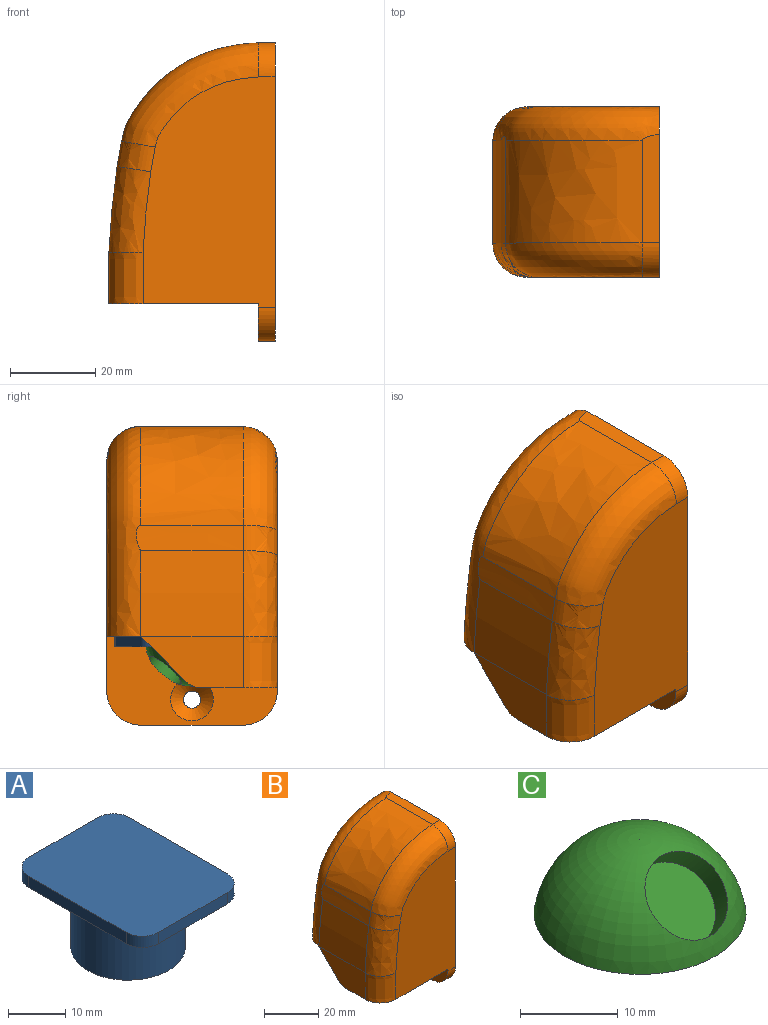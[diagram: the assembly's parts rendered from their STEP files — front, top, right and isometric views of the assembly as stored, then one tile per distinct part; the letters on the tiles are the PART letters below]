
ASSEMBLY  parts=3 mates=2
PART A: 12 faces, bbox 25x32.1x15.4 mm
  f0: cylinder r=10mm len=20mm, axis (0,0,1), area 816.8mm2, adj f1,f7
  f1: plane 20x20mm, normal (0,0,-1), area 314.2mm2, adj f0
  f2: plane 24.05x2.4mm, normal (-1,0,0), area 57.7mm2, adj f6,f7,f8,f11
  f3: plane 17x2.4mm, normal (0,-1,0), area 40.8mm2, adj f6,f7,f8,f9
  f4: plane 24.05x2.4mm, normal (1,0,0), area 57.7mm2, adj f6,f7,f9,f10
  f5: plane 17x2.4mm, normal (0,1,0), area 40.8mm2, adj f6,f7,f10,f11
  f6: plane 32.05x25mm, normal (0,0,1), area 787.5mm2, adj f2,f3,f4,f5,f8,f9,f10,f11
  f7: plane 32.05x25mm, normal (0,0,-1), area 473.4mm2, adj f0,f2,f3,f4,f5,f8,f9,f10
  f8: cylinder r=4mm len=4mm, axis (0,0,-1), area 15.1mm2, adj f2,f3,f6,f7
  f9: cylinder r=4mm len=4mm, axis (0,0,1), area 15.1mm2, adj f3,f4,f6,f7
  f10: cylinder r=4mm len=4mm, axis (0,0,-1), area 15.1mm2, adj f4,f5,f6,f7
  f11: cylinder r=4mm len=4mm, axis (0,0,1), area 15.1mm2, adj f2,f5,f6,f7
PART B: 31 faces, bbox 77.4x46.1x77.5 mm
  f0: plane 39.29x35.29mm, normal (0,0,-1), area 815.2mm2, adj f5,f6,f8,f18,f21,f24,f25,f26
  f1: extruded ~32.04x24mm, area 1015.9mm2, adj f2,f10,f14,f18
  f2: extruded ~24x5.95mm, area 144.9mm2, adj f1,f3,f13,f18
  f3: extruded ~24x20.16mm, area 486.2mm2, adj f2,f12,f18,f23
  f4: plane 54.01x30.99mm, normal (0,-1,0), area 1469.5mm2, adj f8,f11,f12,f13,f14,f15,f17,f22
  f5: plane 54.15x31mm, normal (0,1,0), area 1146.1mm2, adj f0,f8,f11,f16,f18
  f6: cylinder r=10.25mm len=25mm, axis (0,0,-1), area 1610.1mm2, adj f0,f7
  f7: plane 26.63x26.63mm, normal (0,0,-1), area 238mm2, adj f6,f30
  f8: plane 40x20.82mm, normal (-1,0,0), area 628.9mm2, adj f0,f4,f5,f9,f16,f17,f20,f21
  f9: plane 24x4mm, normal (0,0,-1), area 96mm2, adj f8,f11,f16,f17
  f10: plane 26.28x4.75mm, normal (0,0,1), area 100.1mm2, adj f1,f11,f15,f18
  f11: plane 71.39x41.39mm, normal (1,0,0), area 2655mm2, adj f4,f5,f9,f10,f15,f16,f17,f18
  f12: bspline ~23.17x10.11mm, area 248.3mm2, adj f3,f4,f13,f22
  f13: bspline ~9.17x8.61mm, area 74.5mm2, adj f2,f4,f12,f14
  f14: bspline ~68.39x26.56mm, area 480.6mm2, adj f1,f4,f13,f15
  f15: cylinder r=8mm len=8mm, axis (-1,0,0), area 49.3mm2, adj f4,f10,f11,f14
  f16: cylinder r=8mm len=8mm, axis (-1,0,0), area 50.3mm2, adj f5,f8,f9,f11
  f17: cylinder r=8mm len=8mm, axis (1,0,0), area 50.3mm2, adj f4,f8,f9,f11
  f18: bspline ~50.82x40.08mm, area 850.9mm2, adj f0,f1,f2,f3,f5,f10,f11
  f19: cylinder r=2mm len=4mm, axis (1,0,0), area 12.6mm2, adj f11,f20
  f20: cone r=5mm half-angle=45deg, axis (-1,0,0), area 93.3mm2, adj f8,f19
  f21: plane 19.6x12mm, normal (-0.34,0.94,0), area 250.4mm2, adj f0,f8,f26,f27
  f22: extruded ~12x8.01mm, area 150.9mm2, adj f4,f12,f23,f27
  f23: plane 24x12mm, normal (-1,0,0), area 215.5mm2, adj f3,f22,f27,f28,f29
  f24: plane 7.44x7.44mm, normal (1,0,0), area 27.7mm2, adj f0,f25,f28
  f25: plane 23.67x12.11mm, normal (0.94,0.35,0), area 290.6mm2, adj f0,f24,f26,f27,f28,f29
  f26: plane 12x5.49mm, normal (0,1,0), area 65.9mm2, adj f0,f21,f25,f27
  f27: plane 35x17.93mm, normal (0,0,-1), area 204.9mm2, adj f4,f8,f21,f22,f23,f25,f26,f29
  f28: plane 10.54x10.54mm, normal (0,0.71,-0.71), area 17.5mm2, adj f0,f23,f24,f25,f29
  f29: cylinder r=5mm len=3.54mm, axis (-1,0,0), area 11.2mm2, adj f23,f25,f27,f28
  f30: bspline ~24.09x18.61mm, area 749.4mm2, adj f7,f11
PART C: 4 faces, bbox 21.7x21.7x9.3 mm
  f0: plane 21.75x21.75mm, normal (0,0,-1), area 371.4mm2, adj f1
  f1: torus R=0.06mm, axis (0,0,-1), area 565.3mm2, adj f0,f2
  f2: cylinder r=4.82mm len=9.65mm, axis (0,0.64,-0.77), area 86.5mm2, adj f1,f3
  f3: plane 9.65x7.39mm, normal (0,-0.64,0.77), area 73.1mm2, adj f2
PLACE A rot(axis=(0.99,0.17,0),180deg) t=(-16.49,6.93,1.21)mm
PLACE B t=(1.01,6.93,1.21)mm fixed
PLACE C rot(axis=(0.99,0.17,0),180deg) t=(-16.48,6.91,1.26)mm
MATE fastened C.f1 <-> A.f6  axis (0,0,1) through (-16.48,6.91,-1.19)mm
MATE cylindrical B.f6 <-> A.f0  axis (0,0,-1) through (-16.49,6.93,1.21)mm
